# Revit family: Legrand Marina vertical version references 036910 to 036950
name_source: partatom
category: Installations électriques
revit_build: Autodesk Revit 2018 (Build: 20170223_1515(x64)
units: mm (PartAtom-declared; Revit-internal decimal feet)

## family parameters
Basée sur le plan de construction = Non
Conserver l'orientation des annotations = Non
Cote de connecteur circulaire = Utiliser le diamètre
Couper avec des vides une fois chargée = Non
Numéro OmniClass = 23.80.00.00
Partagée = Non
Point de calcul de pièce = Non
Titre OmniClass = Electric Power and Lighting
Toujours verticalement = Oui
Type d'élément = Normal

## types (23) — shared parameters
ETIM Class 6.0 = EC000058
Fabricant = Legrand
General Conditions of Use = https://export.legrand.com
Horizontal version = Non
IK = 10
IP = 66
Material = Metallic
Number of door = 1
RAL = 7035
Square version = Non
URL = www.legrand.fr
Vertical version = Oui

## per-type parameters (varying)
- Legrand Atlantic 036913: Cabinet 036910=Non; Cabinet 036912=Non; Cabinet 036913=Oui; Cabinet 036917=Non; Cabinet 036918=Non; Cabinet 036919=Non; Cabinet 036920=Non; Cabinet 036921=Non; Cabinet 036925=Non; Cabinet 036926=Non; Cabinet 036930=Non; Cabinet 036931=Non; Cabinet 036932=Non; Cabinet 036933=Non; Cabinet 036937=Non; Cabinet 036938=Non; Cabinet 036939=Non; Cabinet 036942=Non; Cabinet 036943=Non; Cabinet 036944=Non; Cabinet 036945=Non; Cabinet 036946=Non; Cabinet 036950=Non; Length=400 mm  [stored 1.31234 ft]; depth=160 mm  [stored 0.524934 ft]; height=500 mm  [stored 1.64042 ft]; weight=9.70 kg
- Legrand Atlantic 036920: Cabinet 036910=Non; Cabinet 036912=Non; Cabinet 036913=Non; Cabinet 036917=Non; Cabinet 036918=Non; Cabinet 036919=Non; Cabinet 036920=Oui; Cabinet 036921=Non; Cabinet 036925=Non; Cabinet 036926=Non; Cabinet 036930=Non; Cabinet 036931=Non; Cabinet 036932=Non; Cabinet 036933=Non; Cabinet 036937=Non; Cabinet 036938=Non; Cabinet 036939=Non; Cabinet 036942=Non; Cabinet 036943=Non; Cabinet 036944=Non; Cabinet 036945=Non; Cabinet 036946=Non; Cabinet 036950=Non; Length=500 mm  [stored 1.64042 ft]; depth=200 mm  [stored 0.656168 ft]; height=600 mm; weight=16.60 kg
- Legrand Atlantic 036921: Cabinet 036910=Non; Cabinet 036912=Non; Cabinet 036913=Non; Cabinet 036917=Non; Cabinet 036918=Non; Cabinet 036919=Non; Cabinet 036920=Non; Cabinet 036921=Oui; Cabinet 036925=Non; Cabinet 036926=Non; Cabinet 036930=Non; Cabinet 036931=Non; Cabinet 036932=Non; Cabinet 036933=Non; Cabinet 036937=Non; Cabinet 036938=Non; Cabinet 036939=Non; Cabinet 036942=Non; Cabinet 036943=Non; Cabinet 036944=Non; Cabinet 036945=Non; Cabinet 036946=Non; Cabinet 036950=Non; Length=500 mm  [stored 1.64042 ft]; depth=200 mm  [stored 0.656168 ft]; height=700 mm  [stored 2.29659 ft]; weight=18.40 kg
- Legrand Atlantic 036942: Cabinet 036910=Non; Cabinet 036912=Non; Cabinet 036913=Non; Cabinet 036917=Non; Cabinet 036918=Non; Cabinet 036919=Non; Cabinet 036920=Non; Cabinet 036921=Non; Cabinet 036925=Non; Cabinet 036926=Non; Cabinet 036930=Non; Cabinet 036931=Non; Cabinet 036932=Non; Cabinet 036933=Non; Cabinet 036937=Non; Cabinet 036938=Non; Cabinet 036939=Non; Cabinet 036942=Oui; Cabinet 036943=Non; Cabinet 036944=Non; Cabinet 036945=Non; Cabinet 036946=Non; Cabinet 036950=Non; Length=600 mm; depth=300 mm; height=1200 mm; weight=47.00 kg
- Legrand Atlantic 036910: Cabinet 036910=Oui; Cabinet 036912=Non; Cabinet 036913=Non; Cabinet 036917=Non; Cabinet 036918=Non; Cabinet 036919=Non; Cabinet 036920=Non; Cabinet 036921=Non; Cabinet 036925=Non; Cabinet 036926=Non; Cabinet 036930=Non; Cabinet 036931=Non; Cabinet 036932=Non; Cabinet 036933=Non; Cabinet 036937=Non; Cabinet 036938=Non; Cabinet 036939=Non; Cabinet 036942=Non; Cabinet 036943=Non; Cabinet 036944=Non; Cabinet 036945=Non; Cabinet 036946=Non; Cabinet 036950=Non; Length=200 mm  [stored 0.656168 ft]; depth=160 mm  [stored 0.524934 ft]; height=300 mm; weight=3.70 kg
- Legrand Atlantic 036912: Cabinet 036910=Non; Cabinet 036912=Oui; Cabinet 036913=Non; Cabinet 036917=Non; Cabinet 036918=Non; Cabinet 036919=Non; Cabinet 036920=Non; Cabinet 036921=Non; Cabinet 036925=Non; Cabinet 036926=Non; Cabinet 036930=Non; Cabinet 036931=Non; Cabinet 036932=Non; Cabinet 036933=Non; Cabinet 036937=Non; Cabinet 036938=Non; Cabinet 036939=Non; Cabinet 036942=Non; Cabinet 036943=Non; Cabinet 036944=Non; Cabinet 036945=Non; Cabinet 036946=Non; Cabinet 036950=Non; Length=300 mm; depth=160 mm  [stored 0.524934 ft]; height=400 mm  [stored 1.31234 ft]; weight=6.30 kg
- Legrand Atlantic 036917: Cabinet 036910=Non; Cabinet 036912=Non; Cabinet 036913=Non; Cabinet 036917=Oui; Cabinet 036918=Non; Cabinet 036919=Non; Cabinet 036920=Non; Cabinet 036921=Non; Cabinet 036925=Non; Cabinet 036926=Non; Cabinet 036930=Non; Cabinet 036931=Non; Cabinet 036932=Non; Cabinet 036933=Non; Cabinet 036937=Non; Cabinet 036938=Non; Cabinet 036939=Non; Cabinet 036942=Non; Cabinet 036943=Non; Cabinet 036944=Non; Cabinet 036945=Non; Cabinet 036946=Non; Cabinet 036950=Non; Length=300 mm; depth=200 mm  [stored 0.656168 ft]; height=400 mm  [stored 1.31234 ft]; weight=6.70 kg
- Legrand Atlantic 036918: Cabinet 036910=Non; Cabinet 036912=Non; Cabinet 036913=Non; Cabinet 036917=Non; Cabinet 036918=Oui; Cabinet 036919=Non; Cabinet 036920=Non; Cabinet 036921=Non; Cabinet 036925=Non; Cabinet 036926=Non; Cabinet 036930=Non; Cabinet 036931=Non; Cabinet 036932=Non; Cabinet 036933=Non; Cabinet 036937=Non; Cabinet 036938=Non; Cabinet 036939=Non; Cabinet 036942=Non; Cabinet 036943=Non; Cabinet 036944=Non; Cabinet 036945=Non; Cabinet 036946=Non; Cabinet 036950=Non; Length=400 mm  [stored 1.31234 ft]; depth=160 mm  [stored 0.524934 ft]; height=500 mm  [stored 1.64042 ft]; weight=10.60 kg
- Legrand Atlantic 036919: Cabinet 036910=Non; Cabinet 036912=Non; Cabinet 036913=Non; Cabinet 036917=Non; Cabinet 036918=Non; Cabinet 036919=Oui; Cabinet 036920=Non; Cabinet 036921=Non; Cabinet 036925=Non; Cabinet 036926=Non; Cabinet 036930=Non; Cabinet 036931=Non; Cabinet 036932=Non; Cabinet 036933=Non; Cabinet 036937=Non; Cabinet 036938=Non; Cabinet 036939=Non; Cabinet 036942=Non; Cabinet 036943=Non; Cabinet 036944=Non; Cabinet 036945=Non; Cabinet 036946=Non; Cabinet 036950=Non; Length=400 mm  [stored 1.31234 ft]; depth=160 mm  [stored 0.524934 ft]; height=600 mm; weight=12.00 kg
- Legrand Atlantic 036925: Cabinet 036910=Non; Cabinet 036912=Non; Cabinet 036913=Non; Cabinet 036917=Non; Cabinet 036918=Non; Cabinet 036919=Non; Cabinet 036920=Non; Cabinet 036921=Non; Cabinet 036925=Oui; Cabinet 036926=Non; Cabinet 036930=Non; Cabinet 036931=Non; Cabinet 036932=Non; Cabinet 036933=Non; Cabinet 036937=Non; Cabinet 036938=Non; Cabinet 036939=Non; Cabinet 036942=Non; Cabinet 036943=Non; Cabinet 036944=Non; Cabinet 036945=Non; Cabinet 036946=Non; Cabinet 036950=Non; Length=400 mm  [stored 1.31234 ft]; depth=250 mm  [stored 0.82021 ft]; height=500 mm  [stored 1.64042 ft]; weight=11.30 kg
- Legrand Atlantic 036926: Cabinet 036910=Non; Cabinet 036912=Non; Cabinet 036913=Non; Cabinet 036917=Non; Cabinet 036918=Non; Cabinet 036919=Non; Cabinet 036920=Non; Cabinet 036921=Non; Cabinet 036925=Non; Cabinet 036926=Oui; Cabinet 036930=Non; Cabinet 036931=Non; Cabinet 036932=Non; Cabinet 036933=Non; Cabinet 036937=Non; Cabinet 036938=Non; Cabinet 036939=Non; Cabinet 036942=Non; Cabinet 036943=Non; Cabinet 036944=Non; Cabinet 036945=Non; Cabinet 036946=Non; Cabinet 036950=Non; Length=400 mm  [stored 1.31234 ft]; depth=250 mm  [stored 0.82021 ft]; height=500 mm  [stored 1.64042 ft]; weight=12.80 kg
- Legrand Atlantic 036930: Cabinet 036910=Non; Cabinet 036912=Non; Cabinet 036913=Non; Cabinet 036917=Non; Cabinet 036918=Non; Cabinet 036919=Non; Cabinet 036920=Non; Cabinet 036921=Non; Cabinet 036925=Non; Cabinet 036926=Non; Cabinet 036930=Oui; Cabinet 036931=Non; Cabinet 036932=Non; Cabinet 036933=Non; Cabinet 036937=Non; Cabinet 036938=Non; Cabinet 036939=Non; Cabinet 036942=Non; Cabinet 036943=Non; Cabinet 036944=Non; Cabinet 036945=Non; Cabinet 036946=Non; Cabinet 036950=Non; Length=500 mm  [stored 1.64042 ft]; depth=250 mm  [stored 0.82021 ft]; height=700 mm  [stored 2.29659 ft]; weight=19.60 kg
- Legrand Atlantic 036931: Cabinet 036910=Non; Cabinet 036912=Non; Cabinet 036913=Non; Cabinet 036917=Non; Cabinet 036918=Non; Cabinet 036919=Non; Cabinet 036920=Non; Cabinet 036921=Non; Cabinet 036925=Non; Cabinet 036926=Non; Cabinet 036930=Non; Cabinet 036931=Oui; Cabinet 036932=Non; Cabinet 036933=Non; Cabinet 036937=Non; Cabinet 036938=Non; Cabinet 036939=Non; Cabinet 036942=Non; Cabinet 036943=Non; Cabinet 036944=Non; Cabinet 036945=Non; Cabinet 036946=Non; Cabinet 036950=Non; Length=600 mm; depth=250 mm  [stored 0.82021 ft]; height=800 mm  [stored 2.62467 ft]; weight=26.60 kg
- Legrand Atlantic 036932: Cabinet 036910=Non; Cabinet 036912=Non; Cabinet 036913=Non; Cabinet 036917=Non; Cabinet 036918=Non; Cabinet 036919=Non; Cabinet 036920=Non; Cabinet 036921=Non; Cabinet 036925=Non; Cabinet 036926=Non; Cabinet 036930=Non; Cabinet 036931=Non; Cabinet 036932=Oui; Cabinet 036933=Non; Cabinet 036937=Non; Cabinet 036938=Non; Cabinet 036939=Non; Cabinet 036942=Non; Cabinet 036943=Non; Cabinet 036944=Non; Cabinet 036945=Non; Cabinet 036946=Non; Cabinet 036950=Non; Length=600 mm; depth=250 mm  [stored 0.82021 ft]; height=1000 mm  [stored 3.28084 ft]; weight=36.20 kg
- Legrand Atlantic 036933: Cabinet 036910=Non; Cabinet 036912=Non; Cabinet 036913=Non; Cabinet 036917=Non; Cabinet 036918=Non; Cabinet 036919=Non; Cabinet 036920=Non; Cabinet 036921=Non; Cabinet 036925=Non; Cabinet 036926=Non; Cabinet 036930=Non; Cabinet 036931=Non; Cabinet 036932=Non; Cabinet 036933=Oui; Cabinet 036937=Non; Cabinet 036938=Non; Cabinet 036939=Non; Cabinet 036942=Non; Cabinet 036943=Non; Cabinet 036944=Non; Cabinet 036945=Non; Cabinet 036946=Non; Cabinet 036950=Non; Length=800 mm  [stored 2.62467 ft]; depth=250 mm  [stored 0.82021 ft]; height=1000 mm  [stored 3.28084 ft]; weight=46.80 kg
- Legrand Atlantic 036937: Cabinet 036910=Non; Cabinet 036912=Non; Cabinet 036913=Non; Cabinet 036917=Non; Cabinet 036918=Non; Cabinet 036919=Non; Cabinet 036920=Non; Cabinet 036921=Non; Cabinet 036925=Non; Cabinet 036926=Non; Cabinet 036930=Non; Cabinet 036931=Non; Cabinet 036932=Non; Cabinet 036933=Non; Cabinet 036937=Oui; Cabinet 036938=Non; Cabinet 036939=Non; Cabinet 036942=Non; Cabinet 036943=Non; Cabinet 036944=Non; Cabinet 036945=Non; Cabinet 036946=Non; Cabinet 036950=Non; Length=600 mm; depth=300 mm; height=800 mm  [stored 2.62467 ft]; weight=28.80 kg
- Legrand Atlantic 036938: Cabinet 036910=Non; Cabinet 036912=Non; Cabinet 036913=Non; Cabinet 036917=Non; Cabinet 036918=Non; Cabinet 036919=Non; Cabinet 036920=Non; Cabinet 036921=Non; Cabinet 036925=Non; Cabinet 036926=Non; Cabinet 036930=Non; Cabinet 036931=Non; Cabinet 036932=Non; Cabinet 036933=Non; Cabinet 036937=Non; Cabinet 036938=Oui; Cabinet 036939=Non; Cabinet 036942=Non; Cabinet 036943=Non; Cabinet 036944=Non; Cabinet 036945=Non; Cabinet 036946=Non; Cabinet 036950=Non; Length=600 mm; depth=300 mm; height=1000 mm  [stored 3.28084 ft]; weight=37.80 kg
- Legrand Atlantic 036939: Cabinet 036910=Non; Cabinet 036912=Non; Cabinet 036913=Non; Cabinet 036917=Non; Cabinet 036918=Non; Cabinet 036919=Non; Cabinet 036920=Non; Cabinet 036921=Non; Cabinet 036925=Non; Cabinet 036926=Non; Cabinet 036930=Non; Cabinet 036931=Non; Cabinet 036932=Non; Cabinet 036933=Non; Cabinet 036937=Non; Cabinet 036938=Non; Cabinet 036939=Oui; Cabinet 036942=Non; Cabinet 036943=Non; Cabinet 036944=Non; Cabinet 036945=Non; Cabinet 036946=Non; Cabinet 036950=Non; Length=800 mm  [stored 2.62467 ft]; depth=300 mm; height=1000 mm  [stored 3.28084 ft]; weight=50.50 kg
- Legrand Atlantic 036943: Cabinet 036910=Non; Cabinet 036912=Non; Cabinet 036913=Non; Cabinet 036917=Non; Cabinet 036918=Non; Cabinet 036919=Non; Cabinet 036920=Non; Cabinet 036921=Non; Cabinet 036925=Non; Cabinet 036926=Non; Cabinet 036930=Non; Cabinet 036931=Non; Cabinet 036932=Non; Cabinet 036933=Non; Cabinet 036937=Non; Cabinet 036938=Non; Cabinet 036939=Non; Cabinet 036942=Non; Cabinet 036943=Oui; Cabinet 036944=Non; Cabinet 036945=Non; Cabinet 036946=Non; Cabinet 036950=Non; Length=800 mm  [stored 2.62467 ft]; depth=300 mm; height=1200 mm; weight=62.20 kg
- Legrand Atlantic 036944: Cabinet 036910=Non; Cabinet 036912=Non; Cabinet 036913=Non; Cabinet 036917=Non; Cabinet 036918=Non; Cabinet 036919=Non; Cabinet 036920=Non; Cabinet 036921=Non; Cabinet 036925=Non; Cabinet 036926=Non; Cabinet 036930=Non; Cabinet 036931=Non; Cabinet 036932=Non; Cabinet 036933=Non; Cabinet 036937=Non; Cabinet 036938=Non; Cabinet 036939=Non; Cabinet 036942=Non; Cabinet 036943=Non; Cabinet 036944=Oui; Cabinet 036945=Non; Cabinet 036946=Non; Cabinet 036950=Non; Length=600 mm; depth=400 mm  [stored 1.31234 ft]; height=800 mm  [stored 2.62467 ft]; weight=36.80 kg
- Legrand Atlantic 036945: Cabinet 036910=Non; Cabinet 036912=Non; Cabinet 036913=Non; Cabinet 036917=Non; Cabinet 036918=Non; Cabinet 036919=Non; Cabinet 036920=Non; Cabinet 036921=Non; Cabinet 036925=Non; Cabinet 036926=Non; Cabinet 036930=Non; Cabinet 036931=Non; Cabinet 036932=Non; Cabinet 036933=Non; Cabinet 036937=Non; Cabinet 036938=Non; Cabinet 036939=Non; Cabinet 036942=Non; Cabinet 036943=Non; Cabinet 036944=Non; Cabinet 036945=Oui; Cabinet 036946=Non; Cabinet 036950=Non; Length=800 mm  [stored 2.62467 ft]; depth=400 mm  [stored 1.31234 ft]; height=1000 mm  [stored 3.28084 ft]; weight=62.30 kg
- Legrand Atlantic 036946: Cabinet 036910=Non; Cabinet 036912=Non; Cabinet 036913=Non; Cabinet 036917=Non; Cabinet 036918=Non; Cabinet 036919=Non; Cabinet 036920=Non; Cabinet 036921=Non; Cabinet 036925=Non; Cabinet 036926=Non; Cabinet 036930=Non; Cabinet 036931=Non; Cabinet 036932=Non; Cabinet 036933=Non; Cabinet 036937=Non; Cabinet 036938=Non; Cabinet 036939=Non; Cabinet 036942=Non; Cabinet 036943=Non; Cabinet 036944=Non; Cabinet 036945=Non; Cabinet 036946=Oui; Cabinet 036950=Non; Length=800 mm  [stored 2.62467 ft]; depth=400 mm  [stored 1.31234 ft]; height=1200 mm; weight=76.00 kg
- Legrand Atlantic 036950: Cabinet 036910=Non; Cabinet 036912=Non; Cabinet 036913=Non; Cabinet 036917=Non; Cabinet 036918=Non; Cabinet 036919=Non; Cabinet 036920=Non; Cabinet 036921=Non; Cabinet 036925=Non; Cabinet 036926=Non; Cabinet 036930=Non; Cabinet 036931=Non; Cabinet 036932=Non; Cabinet 036933=Non; Cabinet 036937=Non; Cabinet 036938=Non; Cabinet 036939=Non; Cabinet 036942=Non; Cabinet 036943=Non; Cabinet 036944=Non; Cabinet 036945=Non; Cabinet 036946=Non; Cabinet 036950=Oui; Length=800 mm  [stored 2.62467 ft]; depth=400 mm  [stored 1.31234 ft]; height=1400 mm  [stored 4.59318 ft]; weight=80.90 kg

note: column(s) folded — value = type name in every type: Description

note: [stored X ft] marks values corroborated as IEEE doubles in the binary element streams (Revit-internal decimal feet)
